# Revit family: IS_Cerabase_BD395_BIM_GB
name_source: partatom
category: Plumbing Fixtures
units: mm (PartAtom-declared; Revit-internal decimal feet)

## family parameters
Cut with Voids When Loaded = No
Host = Face
OmniClass Number = 23.45.55.17
OmniClass Title = Mixing Faucets
Part Type = Normal
Room Calculation Point = No
Round Connector Dimension = Use Diameter
Shared = Yes

## types (1)
- BD395AA - CERABASE BAS H60 CHR BLUE ST,PUW MTL 5L - Crome
    Accessories = https://www.idealstandard.co.uk
    AreaUnits = millimeters
    Assembly Code = C1030200
    AssetType = Fixed
    BIMObjectName = IS_IdealStandard_BasinMixer_Cerabase_BD395
    BIMobject category = Sanitary: Taps & Mixers
    BarCode = 3800861114345
    Brand = Ideal Standard
    Brand url = https://www.idealstandard.co.uk
    CWFU = 0
    Color = Chrome
    ConnectionType = Plumbing
    Cost = 0 $
    Date of publishing = 2023-07-20
    Default Elevation = 800 mm  [stored 2.62467 ft]
    Description = CERABASE - Basin mixer  in chrome finish
    DurationUnit = year
    Edition number = 1
    ExpectedLife = 30
    FaucetFunction = MIXED
    FaucetOperation = LEVERHANDLE
    FaucetType = PILLAR
    Features = CERABASE - Basin mixer  in chrome finish
    Finish = Chrome
    FlowRate = 5 l/min
    GTIN code = 3800861114345
    HWFU = 0
    Help = https://www.idealstandard.co.uk
    IFC Classification = Sanitary Terminal
    IfcExportAs = IfcValveType
    IfcExportType = FAUCET
    InstallationInstructions = https://www.idealstandard.co.uk
    LinearUnits = millimeters
    MAT1 = Chrome_AA
    Manufacturer = Ideal Standard
    Manufacturer name = Ideal Standard
    ManufacturerURL = https://www.idealstandard.co.uk
    Material = Brass
    Material main = Brass
    Model = BD395AA
    ModelNumber = BD395AA
    ModelReference = CERABASE - Basin mixer  in chrome finish
    Name = BasinMixer_Cerabase_BD395_IdealStandard
    NettWeight = 1,24 KG
    NominalHeight = 123 mm
    NominalLength = 153 mm
    NominalWidth = 64 mm
    OmniClass Code = 23-31 11 00 | Faucets
    OmniClass Description = Faucets
    Product SKU = BD395AA
    Product data url = https://www.idealstandard.co.uk
    Product family = CERABASE
    Product name = CERABASE BAS H60 CHR BLUE ST,PUW MTL 5L
    Product url = https://www.idealstandard.co.uk
    ProductInformation = https://www.idealstandard.co.uk
    Shape = Sculptured
    Size = 64 x 153 x 123 mm
    Space = Internal
    SpareParts = https://www.idealstandard.co.uk
    Technical description = CERABASE BAS H60 CHR BLUE ST,PUW MTL 5L
    TestPressure = 10 Bar
    URL = https://www.idealstandard.co.uk
    Uniclass2015Code = Pr_40_20_87_98 | Washbasin taps
    Uniclass2015Description = Washbasin taps
    Uniclass2015Title = Washbasin taps
    Uniclass2015Version = v1.1
    Version = 1
    VolumeUnits = Litres
    WFU = 0
    WRASURL = https://www.wrasapprovals.co.uk
    WarrantyDescription = Manufacturers Warranty
    WarrantyDurationParts = 5
    WarrantyDurationUnit = year
    WarrantyGuarantorParts = https://www.idealstandard.co.uk
    WaterEfficientProduct = No
    WorkingPressure = 3 bar
    Youtube clip = https://www.youtube.com

note: [stored X ft] marks values corroborated as IEEE doubles in the binary element streams (Revit-internal decimal feet)

## geometry (parser evidence)
native form markers: Blend x2, Sweep x2
no freeform markers — native parametric forms only
